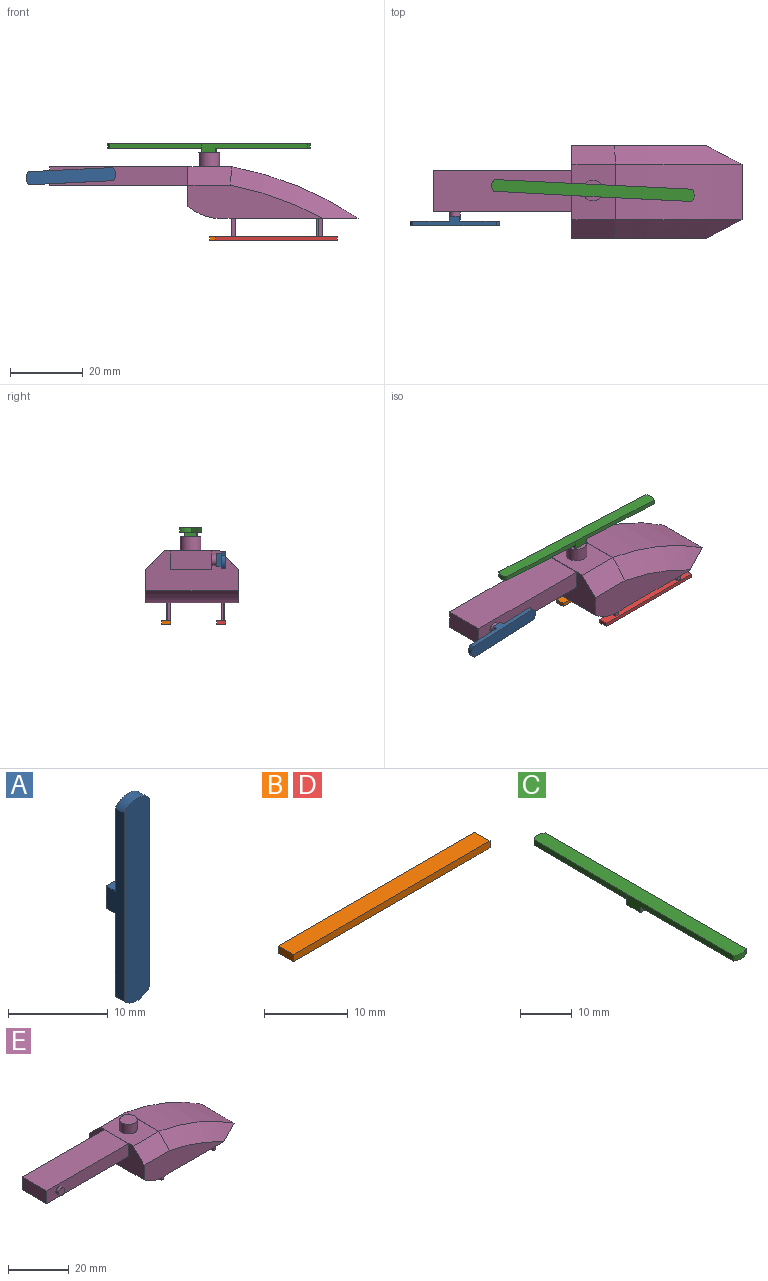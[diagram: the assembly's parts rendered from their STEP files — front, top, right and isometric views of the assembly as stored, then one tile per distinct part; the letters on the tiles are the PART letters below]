
ASSEMBLY  parts=5 mates=4
PART A: 10 faces, bbox 3.6x2.5x24.8 mm
  f0: plane 3.6x1.27mm, normal (0,0,-1), area 4.6mm2, adj f2,f3,f5,f9
  f1: plane 3.6x1.27mm, normal (0,0,1), area 4.6mm2, adj f2,f3,f5,f7
  f2: plane 23.06x2.54mm, normal (-1,0,0), area 32.8mm2, adj f0,f1,f4,f5,f6,f7,f8,f9
  f3: plane 23.06x2.54mm, normal (1,0,0), area 32.8mm2, adj f0,f1,f4,f5,f6,f7,f8,f9
  f4: plane 24.79x3.6mm, normal (0,-1,0), area 87.4mm2, adj f2,f3,f6,f8
  f5: plane 3.6x2.74mm, normal (0,1,0), area 9.9mm2, adj f0,f1,f2,f3
  f6: cylinder r=2.2mm len=3.6mm, axis (0,-1,0), area 5.4mm2, adj f2,f3,f4,f7
  f7: plane 11.09x3.6mm, normal (0,1,0), area 38.9mm2, adj f1,f2,f3,f6
  f8: cylinder r=2.42mm len=3.6mm, axis (0,-1,0), area 5.2mm2, adj f2,f3,f4,f9
  f9: plane 10.96x3.6mm, normal (0,1,0), area 38.6mm2, adj f0,f2,f3,f8
PART B: 6 faces, bbox 33.4x2.5x1 mm
  f0: plane 2.54x1.04mm, normal (-1,0,0), area 2.6mm2, adj f1,f3,f4,f5
  f1: plane 33.35x2.54mm, normal (0,0,-1), area 84.7mm2, adj f0,f2,f4,f5
  f2: plane 2.54x1.04mm, normal (1,0,0), area 2.6mm2, adj f1,f3,f4,f5
  f3: plane 33.35x2.54mm, normal (0,0,1), area 84.7mm2, adj f0,f2,f4,f5
  f4: plane 33.35x1.04mm, normal (0,-1,0), area 34.5mm2, adj f0,f1,f2,f3
  f5: plane 33.35x1.04mm, normal (0,1,0), area 34.5mm2, adj f0,f1,f2,f3
PART C: 11 faces, bbox 3.4x55.8x2.5 mm
  f0: plane 29.21x2.54mm, normal (-1,0,0), area 41.9mm2, adj f1,f3,f4,f5,f6,f7,f9
  f1: plane 3.81x3.37mm, normal (0,0,-1), area 12.8mm2, adj f0,f2,f4,f5
  f2: plane 54.61x2.54mm, normal (1,0,0), area 74.2mm2, adj f1,f3,f4,f5,f6,f7,f8,f10
  f3: plane 55.79x3.37mm, normal (0,0,1), area 184.8mm2, adj f0,f2,f6,f8,f9
  f4: plane 3.37x1.27mm, normal (0,-1,0), area 4.3mm2, adj f0,f1,f2,f7
  f5: plane 3.37x1.27mm, normal (0,1,0), area 4.3mm2, adj f0,f1,f2,f10
  f6: cylinder r=2.89mm len=3.37mm, axis (0,0,1), area 4.6mm2, adj f0,f2,f3,f7
  f7: plane 25.94x3.37mm, normal (0,0,-1), area 86.8mm2, adj f0,f2,f4,f6
  f8: cylinder r=2.34mm len=3.22mm, axis (0,0,1), area 4.5mm2, adj f2,f3,f9,f10
  f9: plane 25.4x1.27mm, normal (-1,0.01,0), area 32.3mm2, adj f0,f3,f8,f10
  f10: plane 26.04x3.37mm, normal (0,0,-1), area 85.1mm2, adj f2,f5,f8,f9
PART D: same geometry as B
PART E: 41 faces, bbox 84.9x25.4x23.1 mm
  f0: plane 25.4x10.99mm, normal (-1,0,0), area 195.4mm2, adj f4,f5,f6,f7,f10,f11,f12,f13
  f1: plane 19.02x1.92mm, normal (-1,0,0), area 0.6mm2, adj f3,f7,f15,f16,f17,f18
  f2: plane 34.88x25.4mm, normal (0,0,-1), area 833.8mm2, adj f3,f4,f5,f6,f16,f18,f22,f23
  f3: cylinder r=93.17mm len=34.88mm, axis (0,1,0), area 577.9mm2, adj f1,f2,f16,f18
  f4: plane 36.99x9.27mm, normal (0,-1,0), area 231.3mm2, adj f0,f2,f6,f17,f18
  f5: plane 36.99x9.27mm, normal (0,1,0), area 231.3mm2, adj f0,f2,f6,f15,f16
  f6: cylinder r=15.1mm len=25.4mm, axis (0,1,0), area 322.7mm2, adj f0,f2,f4,f5,f21,f27
  f7: plane 15.24x11.92mm, normal (0,0,1), area 155.9mm2, adj f0,f1,f8,f15,f17
  f8: cylinder r=2.86mm len=5.73mm, axis (0,0,-1), area 68.5mm2, adj f7,f9
  f9: plane 5.73x5.73mm, normal (0,0,1), area 25.8mm2, adj f8
  f10: plane 38.1x5.12mm, normal (0,-1,0), area 188.4mm2, adj f0,f11,f13,f14,f19
  f11: plane 38.1x11.32mm, normal (0,0,1), area 431.3mm2, adj f0,f10,f12,f14
  f12: plane 38.1x5.12mm, normal (0,1,0), area 195mm2, adj f0,f11,f13,f14
  f13: plane 38.1x11.32mm, normal (0,0,-1), area 431.3mm2, adj f0,f10,f12,f14
  f14: plane 11.32x5.12mm, normal (-1,0,0), area 57.9mm2, adj f10,f11,f12,f13
  f15: plane 11.92x5.08mm, normal (0,0.71,0.71), area 85mm2, adj f0,f1,f5,f7,f16
  f16: cone r=93.17mm half-angle=45deg, axis (0,-1,0), area 233.7mm2, adj f1,f2,f3,f5,f15
  f17: plane 11.92x5.08mm, normal (0,-0.71,0.71), area 85mm2, adj f0,f1,f4,f7,f18
  f18: cone r=88.09mm half-angle=45deg, axis (0,1,0), area 233.7mm2, adj f1,f2,f3,f4,f17
  f19: cylinder r=1.45mm len=2.9mm, axis (0,1,0), area 11.6mm2, adj f10,f20
  f20: plane 2.9x2.9mm, normal (0,-1,0), area 6.6mm2, adj f19
  f21: plane 5.08x0.7mm, normal (-1,0,0), area 3.6mm2, adj f6,f22,f24,f25
  f22: plane 5.08x1.08mm, normal (0,1,0), area 5.5mm2, adj f2,f21,f23,f25
  f23: plane 5.08x0.7mm, normal (1,0,0), area 3.6mm2, adj f2,f22,f24,f25
  f24: plane 5.08x1.08mm, normal (0,-1,0), area 5.5mm2, adj f2,f21,f23,f25
  f25: plane 1.08x0.7mm, normal (0,0,-1), area 0.8mm2, adj f21,f22,f23,f24
  f26: plane 5.08x1.11mm, normal (0,-1,0), area 5.6mm2, adj f2,f27,f29,f30
  f27: plane 5.08x0.86mm, normal (-1,0,0), area 4.4mm2, adj f6,f26,f28,f30
  f28: plane 5.08x1.11mm, normal (0,1,0), area 5.6mm2, adj f2,f27,f29,f30
  f29: plane 5.08x0.86mm, normal (1,0,0), area 4.4mm2, adj f2,f26,f28,f30
  f30: plane 1.11x0.86mm, normal (0,0,-1), area 1mm2, adj f26,f27,f28,f29
  f31: plane 5.08x1.18mm, normal (0,-1,0), area 6mm2, adj f2,f32,f34,f35
  f32: plane 5.08x0.83mm, normal (-1,0,0), area 4.2mm2, adj f2,f31,f33,f35
  f33: plane 5.08x1.18mm, normal (0,1,0), area 6mm2, adj f2,f32,f34,f35
  f34: plane 5.08x0.83mm, normal (1,0,0), area 4.2mm2, adj f2,f31,f33,f35
  f35: plane 1.18x0.83mm, normal (0,0,-1), area 1mm2, adj f31,f32,f33,f34
  f36: plane 5.08x0.76mm, normal (-1,0,0), area 3.9mm2, adj f2,f37,f39,f40
  f37: plane 5.08x1.27mm, normal (0,1,0), area 6.5mm2, adj f2,f36,f38,f40
  f38: plane 5.08x0.76mm, normal (1,0,0), area 3.9mm2, adj f2,f37,f39,f40
  f39: plane 5.08x1.27mm, normal (0,-1,0), area 6.5mm2, adj f2,f36,f38,f40
  f40: plane 1.27x0.76mm, normal (0,0,-1), area 1mm2, adj f36,f37,f38,f39
PLACE A rot(axis=(0,1,0),87.2deg) t=(-77,-9.02,-16.46)mm
PLACE B t=(6.32,6.06,21.05)mm
PLACE C rot(axis=(0,0,1),87.2deg) t=(-7.13,3.68,-0.32)mm
PLACE D t=(7.95,-9.1,21.05)mm
PLACE E t=(0.6,10.41,12.04)mm fixed
MATE revolute E.f8 <-> C.f1  axis (0,0,1) through (-5.5,-1.91,30.01)mm
MATE revolute E.f19 <-> A.f5  axis (0,-1,0) through (-43.59,-9.02,23.59)mm
MATE fastened B.f3 <-> E.f30  axis (0,0,1) through (11.39,4.79,6.96)mm
MATE fastened E.f35 <-> D.f3  axis (0,0,1) through (25.72,-10.37,6.96)mm
